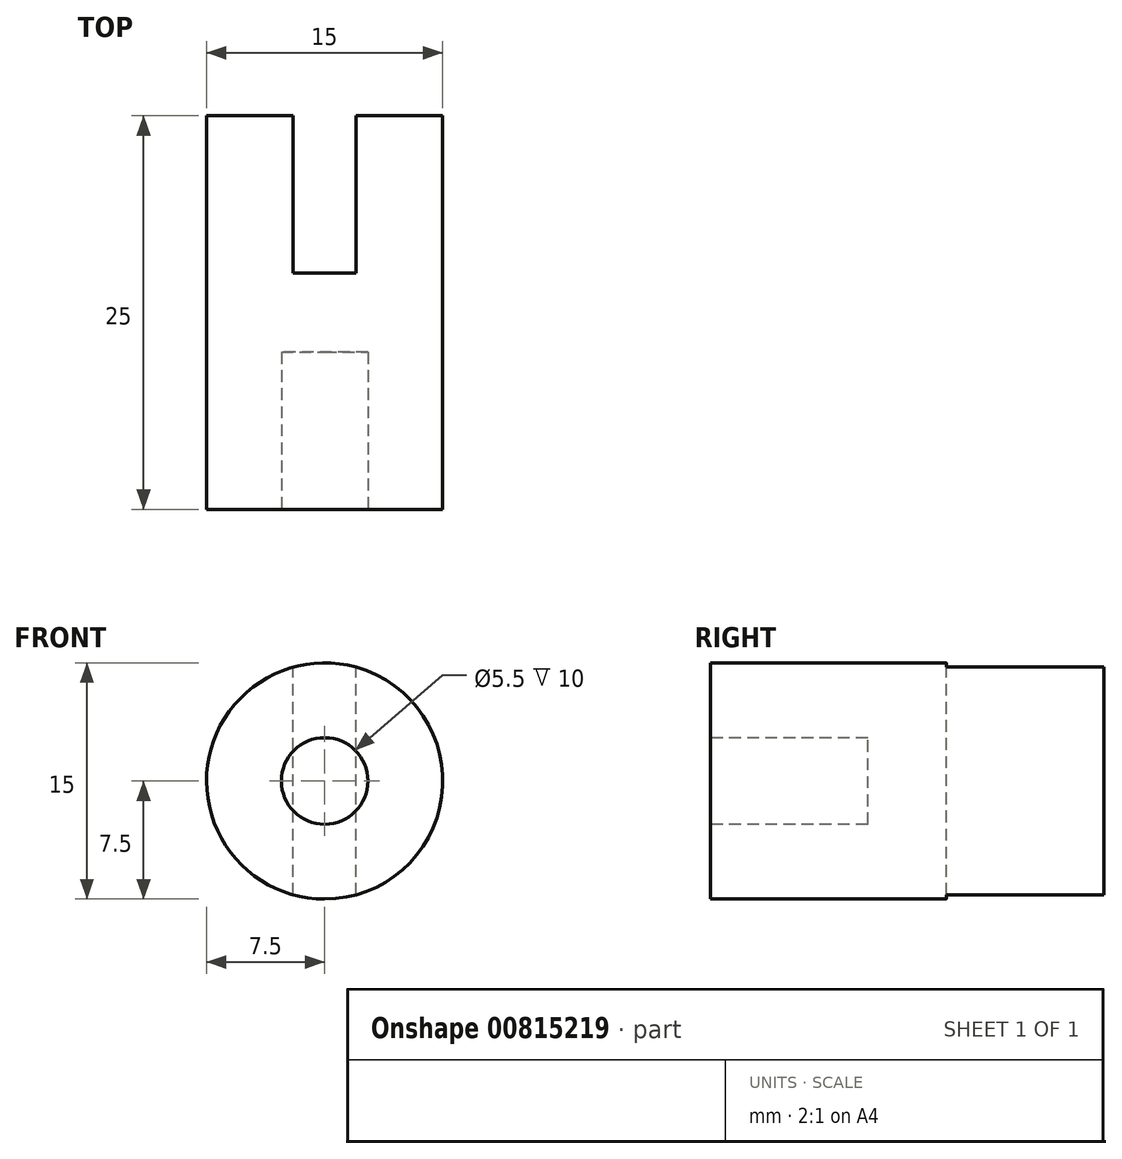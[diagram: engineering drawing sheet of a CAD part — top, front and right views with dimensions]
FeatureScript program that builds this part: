
annotation { "Feature Type Name" : "Feature", "Feature Type Description" : "" }
export const myFeature = defineFeature(function(context is Context, id is Id, definition is map)
    precondition{}
    {
        {
            var Q0;
            Q0=qCreatedBy(makeId("Front.planeOp"),FACE);
            var sketch = newSketch(context, id + "F0", { "sketchPlane" : qUnion([Q0])});
            skCircle(sketch, "E0", {"center": v(0, 0) * mm, "radius": 7.5 * mm});
            skSolve(sketch);
        }
        {
            var Q0;
            Q0 = qSketchRegion(id + "F0", true);
            extrude(context, id + "F1", {"entities" : qUnion([Q0]), "depth" : 25 * mm, "offsetDistance" : 25 * mm});
        }
        {
            var Q0;
            Q0=makeQuery(id+"F1.opExtrude","CAP_FACE",FACE,{"disambiguationData":[OSD([sQuery(id+"F0.wireOp",EDGE,"E0")])],"isStart":false});
            var sketch = newSketch(context, id + "F2", { "sketchPlane" : qUnion([Q0])});
            skCircle(sketch, "E1", {"center": v(0, 0) * mm, "radius": 2.75 * mm});
            skSolve(sketch);
        }
        {
            var Q0;
            Q0=makeQuery(id+"F2.imprint","IMPRINT",FACE,{"disambiguationData":[TD([[makeQuery(id+"F2.imprint","IMPRINT",EDGE,{"derivedFrom":sQuery(id+"F2.wireOp",EDGE,"E1")}),1.0]])]});
            extrude(context, id + "F3", {"entities" : qUnion([Q0]), "operationType" : NewBodyOperationType.REMOVE, "oppositeDirection" : true, "depth" : 10 * mm, "offsetDistance" : 25 * mm});
        }
        {
            var Q0;
            Q0=makeQuery(id+"F1.opExtrude","CAP_FACE",FACE,{"disambiguationData":[OSD([sQuery(id+"F0.wireOp",EDGE,"E0")])],"isStart":true});
            var sketch = newSketch(context, id + "F4", { "sketchPlane" : qUnion([Q0])});
            skLineSegment(sketch, "E2.bottom", {"start": v(2, -7.5) * mm, "end": v(-2, -7.5) * mm});
            skLineSegment(sketch, "E2.top", {"start": v(2, 7.5) * mm, "end": v(-2, 7.5) * mm});
            skLineSegment(sketch, "E2.left", {"start": v(2, -7.5) * mm, "end": v(2, 7.5) * mm});
            skLineSegment(sketch, "E2.right", {"start": v(-2, -7.5) * mm, "end": v(-2, 7.5) * mm});
            skPoint(sketch, "E2.middle", {"position": v(0, 0) * mm});
            skSolve(sketch);
        }
        {
            var Q0;
            Q0 = qSketchRegion(id + "F4", true);
            extrude(context, id + "F5", {"entities" : qUnion([Q0]), "operationType" : NewBodyOperationType.REMOVE, "oppositeDirection" : true, "depth" : 10 * mm, "offsetDistance" : 25 * mm});
        }
    });
